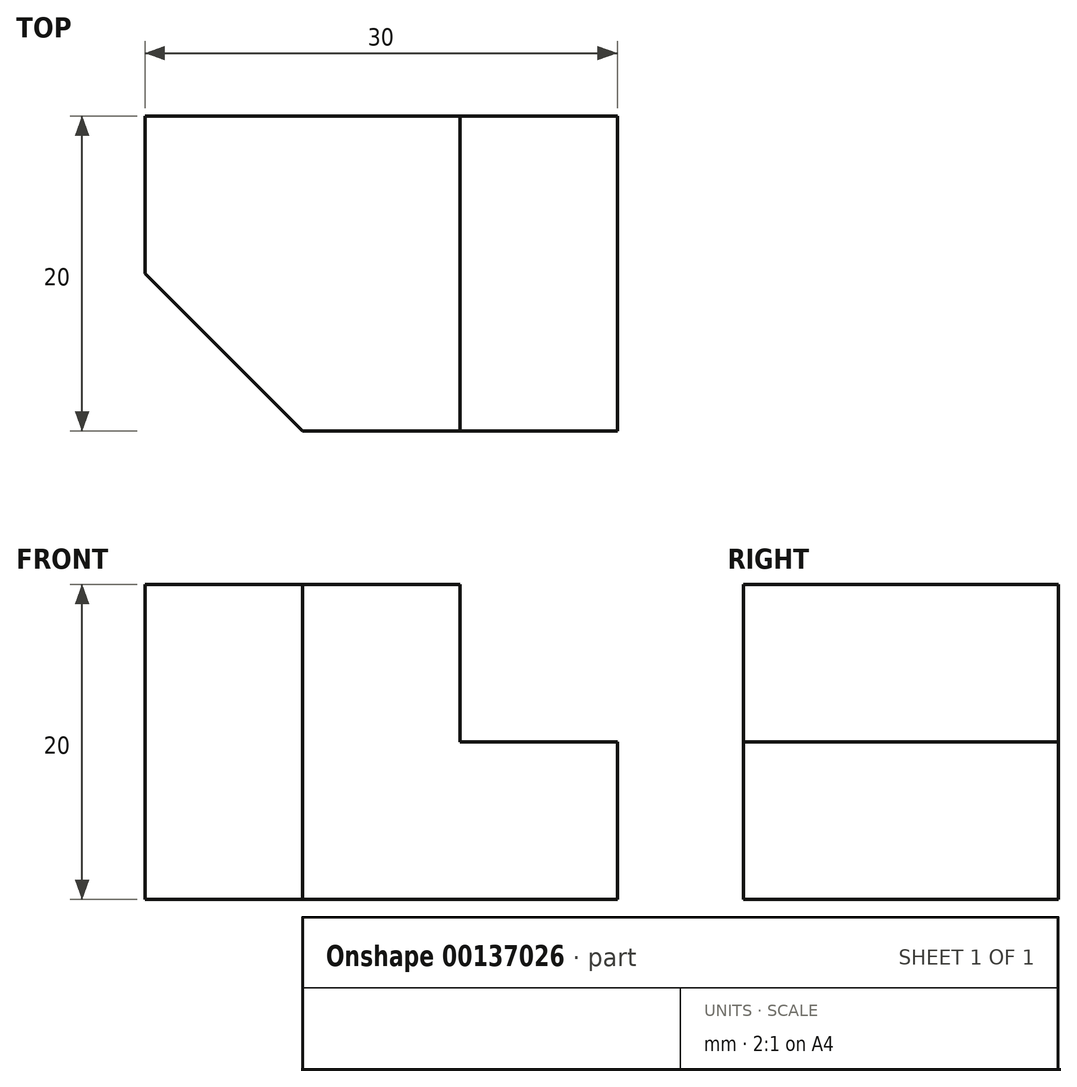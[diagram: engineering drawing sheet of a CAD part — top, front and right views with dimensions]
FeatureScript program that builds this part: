
annotation { "Feature Type Name" : "Feature", "Feature Type Description" : "" }
export const myFeature = defineFeature(function(context is Context, id is Id, definition is map)
    precondition{}
    {
        {
            var Q0;
            Q0=qCreatedBy(makeId("Front.planeOp"),FACE);
            var sketch = newSketch(context, id + "F0", { "sketchPlane" : qUnion([Q0])});
            skLineSegment(sketch, "E0.bottom", {"start": v(0, 0) * mm, "end": v(30, 0) * mm});
            skLineSegment(sketch, "E0.top", {"start": v(0, 20) * mm, "end": v(20, 20) * mm});
            skLineSegment(sketch, "E0.left", {"start": v(0, 0) * mm, "end": v(0, 20) * mm});
            skLineSegment(sketch, "E0.right", {"start": v(30, 0) * mm, "end": v(30, 10) * mm});
            skLineSegment(sketch, "E1", {"start": v(20, 20) * mm, "end": v(20, 10) * mm});
            skPoint(sketch, "E1.endSnap0", {"position": v(0, 10) * mm});
            skLineSegment(sketch, "E2", {"start": v(20, 10) * mm, "end": v(30, 10) * mm});
            skPoint(sketch, "E3.orphan", {"position": v(30, 20) * mm});
            skSolve(sketch);
        }
        {
            var Q0;
            Q0=makeQuery(id+"F0.imprint","IMPRINT",FACE,{"disambiguationData":[TD([[makeQuery(id+"F0.imprint","IMPRINT",EDGE,{"derivedFrom":sQuery(id+"F0.wireOp",EDGE,"E0.bottom")}),1.0]])]});
            extrude(context, id + "F1", {"entities" : qUnion([Q0]), "oppositeDirection" : true, "depth" : 20 * mm});
        }
        {
            var Q0;
            Q0=makeQuery(id+"F1.opExtrude","SWEPT_FACE",FACE,{"disambiguationData":[OSD([sQuery(id+"F0.wireOp",EDGE,"E0.top")])]});
            var sketch = newSketch(context, id + "F2", { "sketchPlane" : qUnion([Q0])});
            skLineSegment(sketch, "E4.bottom", {"start": v(0, 0) * mm, "end": v(20, 0) * mm, "construction": true});
            skLineSegment(sketch, "E4.top", {"start": v(0, 20) * mm, "end": v(20, 20) * mm, "construction": true});
            skLineSegment(sketch, "E4.left", {"start": v(0, 0) * mm, "end": v(0, 20) * mm, "construction": true});
            skLineSegment(sketch, "E4.right", {"start": v(20, 0) * mm, "end": v(20, 20) * mm, "construction": true});
            skLineSegment(sketch, "E5", {"start": v(0, 0) * mm, "end": v(0, 10) * mm});
            skLineSegment(sketch, "E6", {"start": v(0, 10) * mm, "end": v(10, 0) * mm});
            skLineSegment(sketch, "E7", {"start": v(10, 0) * mm, "end": v(0, 0) * mm});
            skSolve(sketch);
        }
        {
            var Q0;
            Q0=makeQuery(id+"F2.imprint","IMPRINT",FACE,{"disambiguationData":[TD([[makeQuery(id+"F2.imprint","IMPRINT",EDGE,{"derivedFrom":sQuery(id+"F2.wireOp",EDGE,"E5")}),1.0]])]});
            extrude(context, id + "F3", {"entities" : qUnion([Q0]), "operationType" : NewBodyOperationType.REMOVE, "oppositeDirection" : true, "depth" : 20 * mm});
        }
    });
